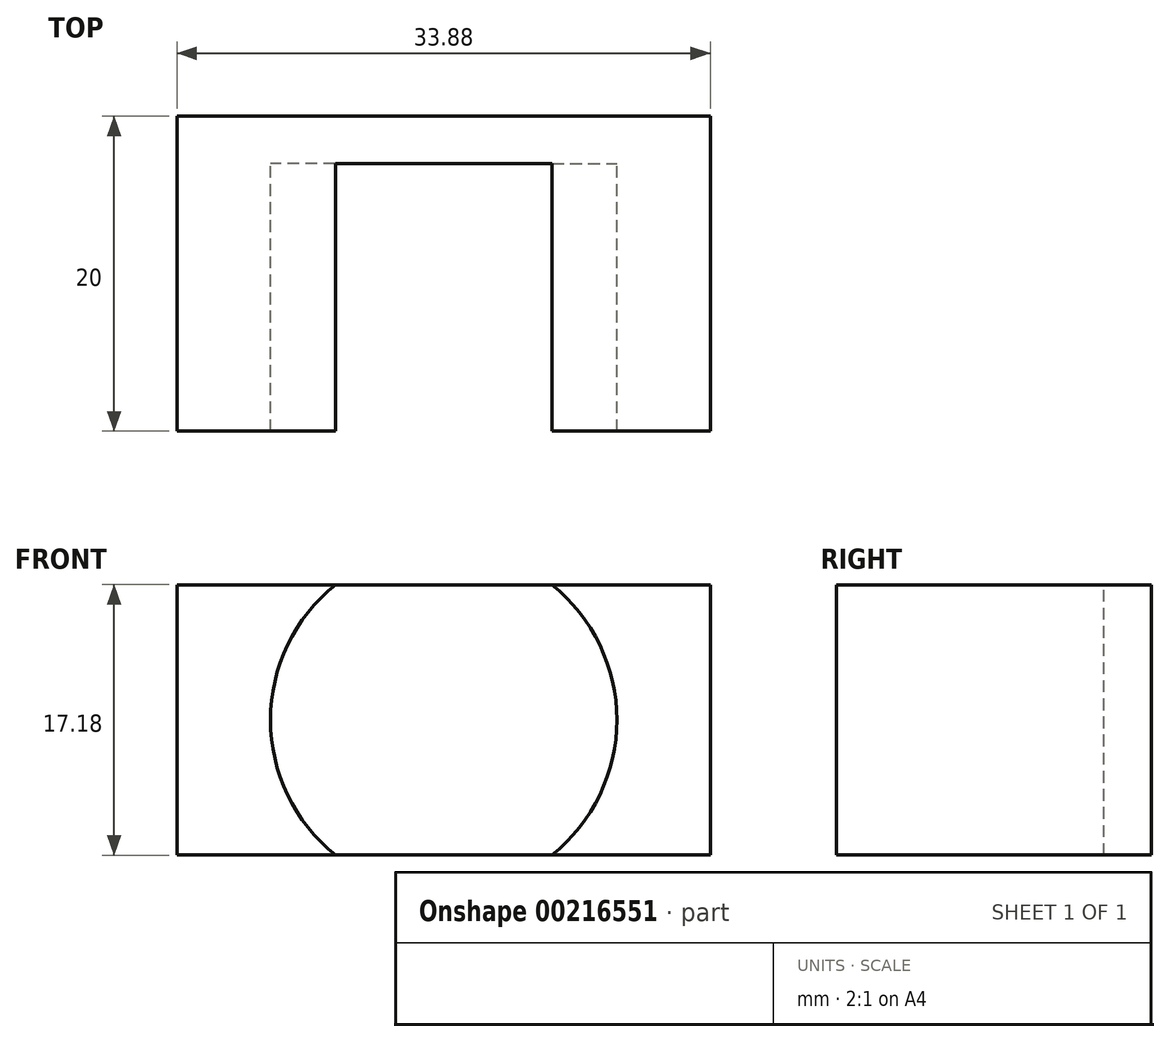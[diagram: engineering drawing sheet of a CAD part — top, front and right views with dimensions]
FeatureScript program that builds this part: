
annotation { "Feature Type Name" : "Feature", "Feature Type Description" : "" }
export const myFeature = defineFeature(function(context is Context, id is Id, definition is map)
    precondition{}
    {
        {
            var Q0;
            Q0=qCreatedBy(makeId("Front.planeOp"),FACE);
            var sketch = newSketch(context, id + "F0", { "sketchPlane" : qUnion([Q0])});
            skArc(sketch, "E0", {"start": v(-6.88, 8.59) * mm, "mid": v(-11, 0) * mm, "end": v(-6.88, -8.59) * mm});
            skLineSegment(sketch, "E1.bottom", {"start": v(16.94, -8.59) * mm, "end": v(-16.94, -8.59) * mm});
            skLineSegment(sketch, "E1.top", {"start": v(16.94, 8.59) * mm, "end": v(-16.94, 8.59) * mm});
            skLineSegment(sketch, "E1.left", {"start": v(16.94, -8.59) * mm, "end": v(16.94, 8.59) * mm});
            skLineSegment(sketch, "E1.right", {"start": v(-16.94, -8.59) * mm, "end": v(-16.94, 8.59) * mm});
            skArc(sketch, "E2.trimOffspring", {"start": v(6.88, -8.59) * mm, "mid": v(11, 0) * mm, "end": v(6.88, 8.59) * mm});
            skSolve(sketch);
        }
        {
            var Q0;
            {var subQ0=sQuery(id+"F0.wireOp",EDGE,"E0");Q0=makeQuery(id+"F0.imprint","IMPRINT",FACE,{"disambiguationData":[TD([[makeQuery(id+"F0.imprint","IMPRINT",EDGE,{"derivedFrom":subQ0}),1.0]])]});}
            extrude(context, id + "F1", {"entities" : qUnion([Q0]), "depth" : 3 * mm});
        }
        {
            var Q0;
            {var subQ0=sQuery(id+"F0.wireOp",EDGE,"E0");Q0=makeQuery(id+"F0.imprint","IMPRINT",FACE,{"disambiguationData":[TD([[makeQuery(id+"F0.imprint","IMPRINT",EDGE,{"derivedFrom":subQ0}),-1.0]])]});}
            var Q1;
            {var subQ0=sQuery(id+"F0.wireOp",EDGE,"E1.left");Q1=makeQuery(id+"F0.imprint","IMPRINT",FACE,{"disambiguationData":[TD([[makeQuery(id+"F0.imprint","IMPRINT",EDGE,{"derivedFrom":subQ0}),1.0]])]});}
            extrude(context, id + "F2", {"entities" : qUnion([Q0, Q1]), "operationType" : NewBodyOperationType.ADD, "depth" : 20 * mm});
        }
    });
